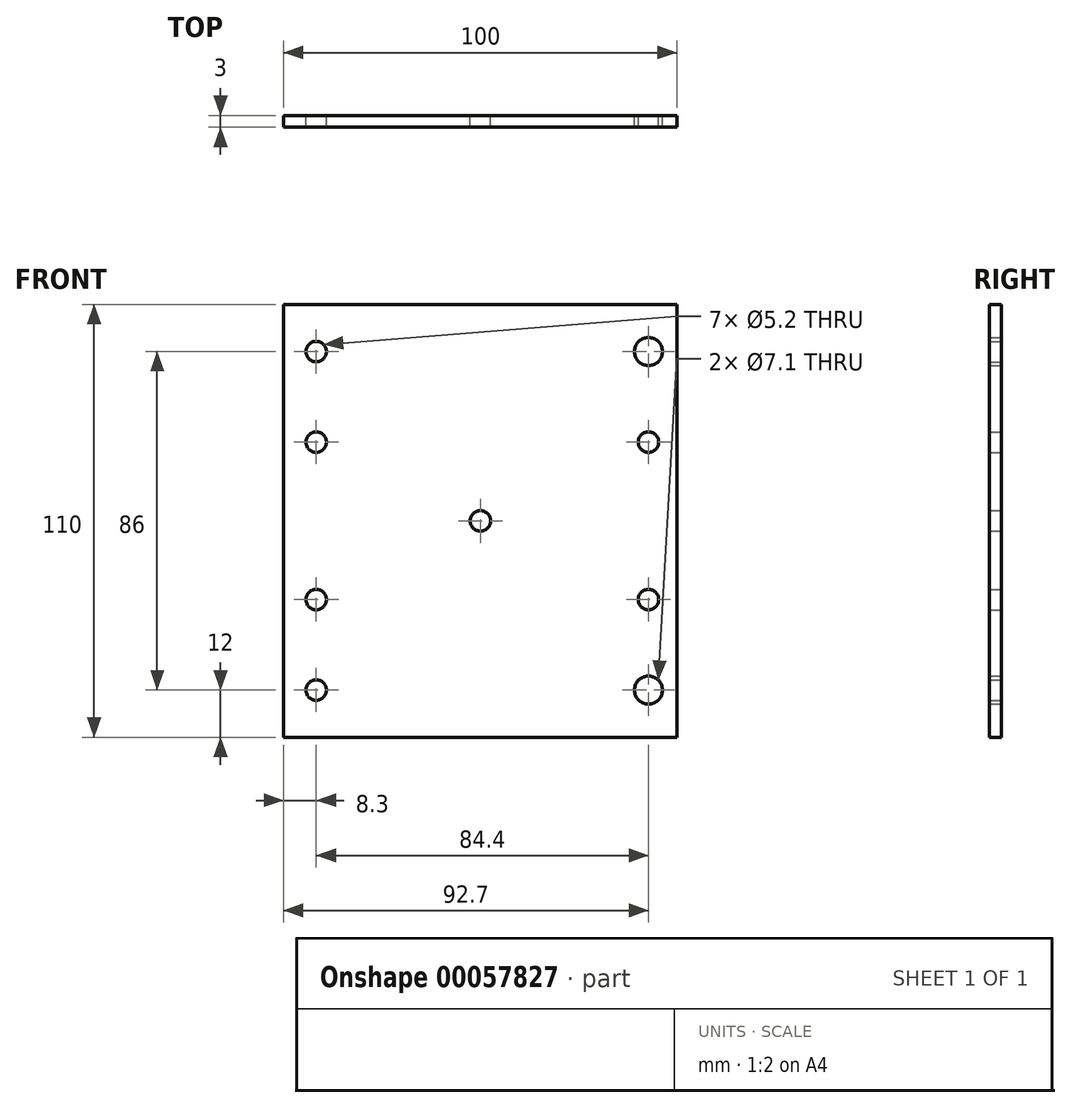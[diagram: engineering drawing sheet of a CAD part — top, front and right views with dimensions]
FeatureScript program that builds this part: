
annotation { "Feature Type Name" : "Feature", "Feature Type Description" : "" }
export const myFeature = defineFeature(function(context is Context, id is Id, definition is map)
    precondition{}
    {
        {
            var Q0;
            Q0=qCreatedBy(makeId("Front.planeOp"),FACE);
            var sketch = newSketch(context, id + "F0", { "sketchPlane" : qUnion([Q0])});
            skLineSegment(sketch, "E0.bottom", {"start": v(-50, 55) * mm, "end": v(50, 55) * mm});
            skLineSegment(sketch, "E0.top", {"start": v(-50, -55) * mm, "end": v(50, -55) * mm});
            skLineSegment(sketch, "E0.left", {"start": v(-50, 55) * mm, "end": v(-50, -55) * mm});
            skLineSegment(sketch, "E0.right", {"start": v(50, 55) * mm, "end": v(50, -55) * mm});
            skPoint(sketch, "E0.middle", {"position": v(0, 0) * mm});
            skLineSegment(sketch, "E1", {"start": v(-41.7, 55) * mm, "end": v(-41.7, -55) * mm, "construction": true});
            skLineSegment(sketch, "E2", {"start": v(0, 0) * mm, "end": v(0, -68.3) * mm, "construction": true});
            skPoint(sketch, "E2.endSnap0", {"position": v(0, -55) * mm});
            skLineSegment(sketch, "E3.MirrorCS", {"start": v(41.7, 55) * mm, "end": v(41.7, -55) * mm, "construction": true});
            skLineSegment(sketch, "E4", {"start": v(42.7, 55) * mm, "end": v(42.7, -55) * mm, "construction": true});
            skLineSegment(sketch, "E5", {"start": v(-50, 43) * mm, "end": v(50, 43) * mm, "construction": true});
            skLineSegment(sketch, "E6", {"start": v(0, 0) * mm, "end": v(34.57, 0) * mm, "construction": true});
            skLineSegment(sketch, "E7.MirrorCS", {"start": v(-50, -43) * mm, "end": v(50, -43) * mm, "construction": true});
            skPoint(sketch, "E8", {"position": v(-41.7, 43) * mm});
            skPoint(sketch, "E9", {"position": v(42.7, 43) * mm});
            skPoint(sketch, "E10", {"position": v(-41.7, -43) * mm});
            skPoint(sketch, "E11", {"position": v(42.7, -43) * mm});
            skCircle(sketch, "E12", {"center": v(-41.7, -43) * mm, "radius": 2.6 * mm});
            skCircle(sketch, "E13", {"center": v(-41.7, 43) * mm, "radius": 2.6 * mm});
            skCircle(sketch, "E14", {"center": v(42.7, -43) * mm, "radius": 3.55 * mm});
            skCircle(sketch, "E15", {"center": v(42.7, 43) * mm, "radius": 3.55 * mm});
            skCircle(sketch, "E16", {"center": v(-41.7, 43) * mm, "radius": 8.66 * mm, "construction": true});
            skCircle(sketch, "E17", {"center": v(-41.7, -43) * mm, "radius": 8.66 * mm, "construction": true});
            skPoint(sketch, "E18", {"position": v(41.7, -43) * mm});
            skPoint(sketch, "E19", {"position": v(41.7, 43) * mm});
            skCircle(sketch, "E20", {"center": v(41.7, 43) * mm, "radius": 8.66 * mm, "construction": true});
            skCircle(sketch, "E21", {"center": v(41.7, -43) * mm, "radius": 8.66 * mm, "construction": true});
            skCircle(sketch, "E22", {"center": v(0, 0) * mm, "radius": 2.6 * mm});
            skLineSegment(sketch, "E23.bottom", {"start": v(-41.7, -20) * mm, "end": v(41.7, -20) * mm, "construction": true});
            skLineSegment(sketch, "E23.top", {"start": v(-41.7, 20) * mm, "end": v(41.7, 20) * mm, "construction": true});
            skLineSegment(sketch, "E23.left", {"start": v(-41.7, -20) * mm, "end": v(-41.7, 20) * mm});
            skLineSegment(sketch, "E23.right", {"start": v(41.7, -20) * mm, "end": v(41.7, 20) * mm});
            skPoint(sketch, "E24", {"position": v(42.7, 20) * mm});
            skPoint(sketch, "E25", {"position": v(42.7, -20) * mm});
            skCircle(sketch, "E26", {"center": v(-41.7, 20) * mm, "radius": 2.6 * mm});
            skCircle(sketch, "E27", {"center": v(42.7, 20) * mm, "radius": 2.6 * mm});
            skCircle(sketch, "E28", {"center": v(-41.7, -20) * mm, "radius": 2.6 * mm});
            skCircle(sketch, "E29", {"center": v(42.7, -20) * mm, "radius": 2.6 * mm});
            skSolve(sketch);
        }
        {
            var Q0;
            Q0 = qSketchRegion(id + "F0", true);
            extrude(context, id + "F1", {"entities" : qUnion([Q0]), "depth" : 3 * mm, "offsetDistance" : 25 * mm});
        }
    });
